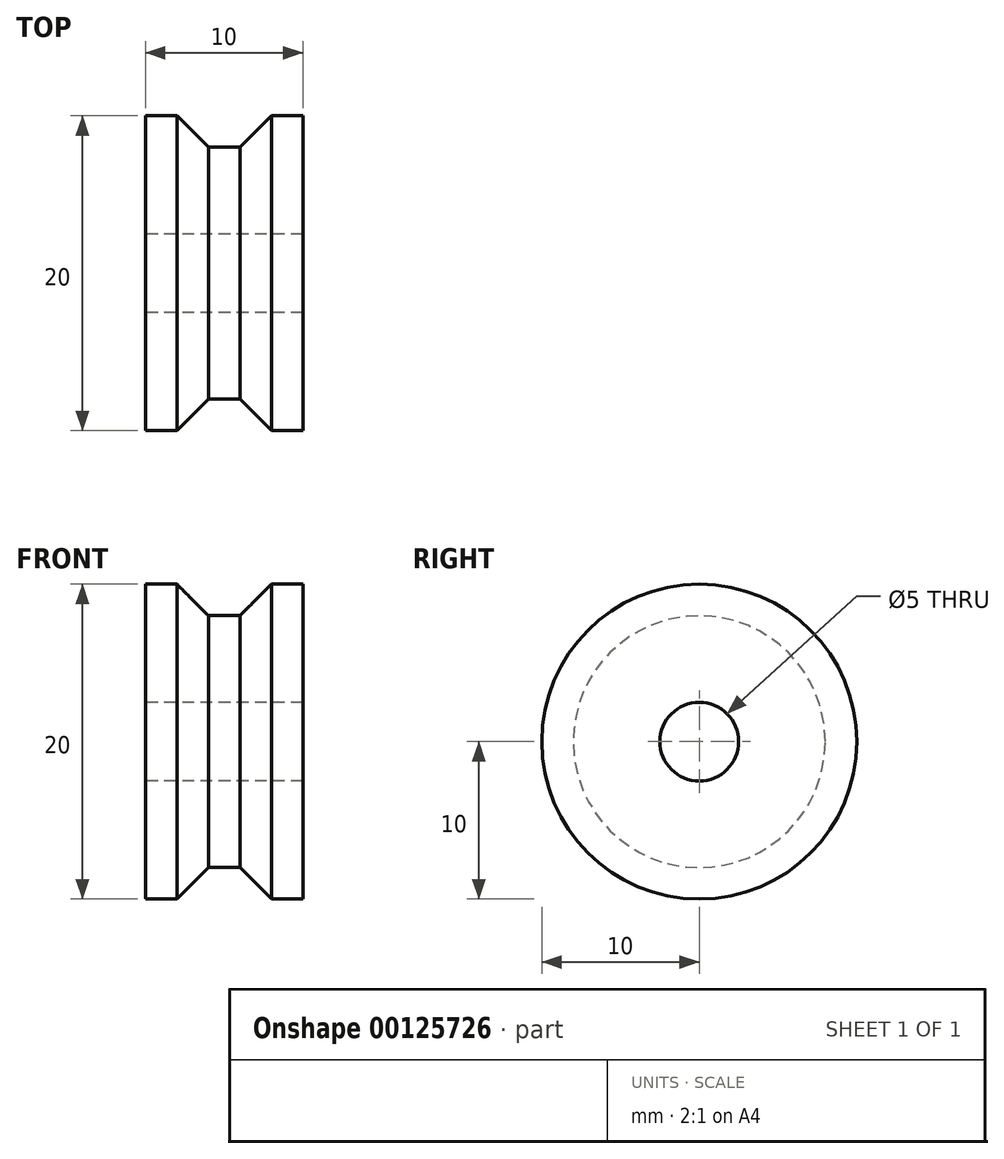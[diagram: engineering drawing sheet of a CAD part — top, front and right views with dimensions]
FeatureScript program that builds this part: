
annotation { "Feature Type Name" : "Feature", "Feature Type Description" : "" }
export const myFeature = defineFeature(function(context is Context, id is Id, definition is map)
    precondition{}
    {
        {
            var Q0;
            Q0=qCreatedBy(makeId("Front.planeOp"),FACE);
            var sketch = newSketch(context, id + "F0", { "sketchPlane" : qUnion([Q0])});
            skLineSegment(sketch, "E0", {"start": v(1, 8) * mm, "end": v(3, 10) * mm});
            skLineSegment(sketch, "E1", {"start": v(3, 10) * mm, "end": v(5, 10) * mm});
            skLineSegment(sketch, "E2", {"start": v(5, 10) * mm, "end": v(5, 0) * mm});
            skLineSegment(sketch, "E3.MirrorCS", {"start": v(-1, 8) * mm, "end": v(-3, 10) * mm});
            skLineSegment(sketch, "E4.MirrorCS", {"start": v(-3, 10) * mm, "end": v(-5, 10) * mm});
            skLineSegment(sketch, "E5.MirrorCS", {"start": v(-5, 10) * mm, "end": v(-5, 0) * mm});
            skLineSegment(sketch, "E6", {"start": v(-5, 0) * mm, "end": v(5, 0) * mm});
            skLineSegment(sketch, "E7", {"start": v(-1, 8) * mm, "end": v(1, 8) * mm});
            skSolve(sketch);
        }
        {
            var Q0;
            Q0=makeQuery(id+"F0.imprint","IMPRINT",FACE,{"disambiguationData":[TD([[makeQuery(id+"F0.imprint","IMPRINT",EDGE,{"derivedFrom":sQuery(id+"F0.wireOp",EDGE,"E0")}),-1.0]])]});
            var Q1;
            Q1=sQuery(id+"F0.wireOp",EDGE,"E6");
            revolve(context, id + "F1", {"entities" : qUnion([Q0]), "axis" : qUnion([Q1]), "revolveType" : RevolveType.FULL});
        }
        {
            var Q0;
            Q0=makeQuery(id+"F1.opRevolve","SWEPT_FACE",FACE,{"disambiguationData":[OSD([sQuery(id+"F0.wireOp",EDGE,"E5.MirrorCS")])]});
            var sketch = newSketch(context, id + "F2", { "sketchPlane" : qUnion([Q0])});
            skCircle(sketch, "E8", {"center": v(0, 0) * mm, "radius": 2.5 * mm});
            skSolve(sketch);
        }
        {
            var Q0;
            Q0=makeQuery(id+"F2.imprint","IMPRINT",FACE,{"disambiguationData":[TD([[makeQuery(id+"F2.imprint","IMPRINT",EDGE,{"derivedFrom":sQuery(id+"F2.wireOp",EDGE,"E8")}),1.0]])]});
            extrude(context, id + "F3", {"entities" : qUnion([Q0]), "operationType" : NewBodyOperationType.REMOVE, "endBound" : BoundingType.UP_TO_NEXT, "oppositeDirection" : true, "depth" : 25 * mm});
        }
    });
